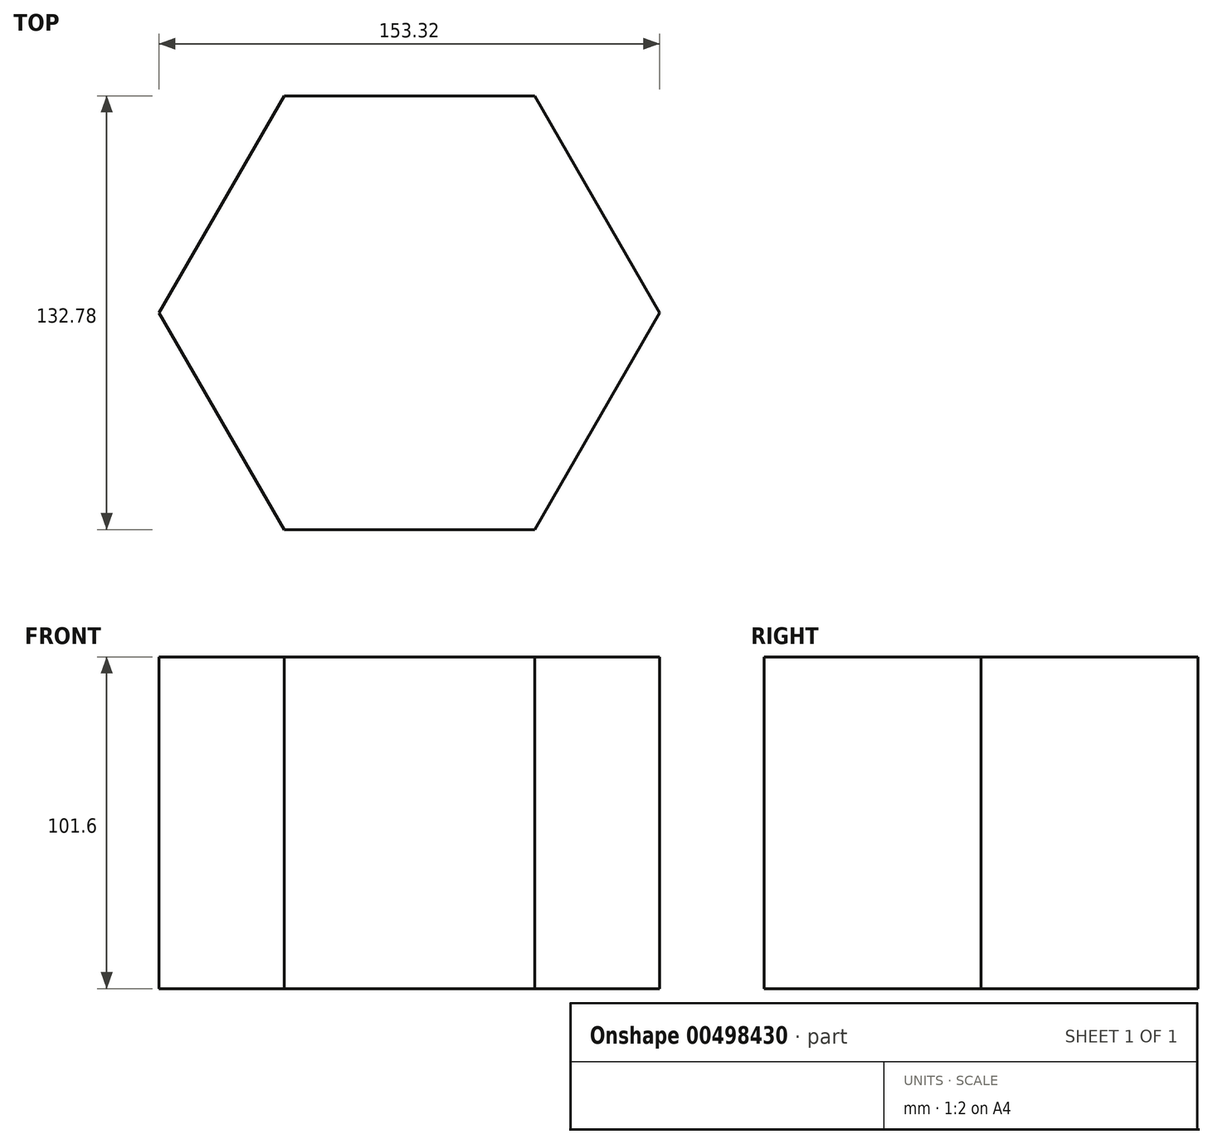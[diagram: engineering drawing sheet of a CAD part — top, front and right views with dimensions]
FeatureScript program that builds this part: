
annotation { "Feature Type Name" : "Feature", "Feature Type Description" : "" }
export const myFeature = defineFeature(function(context is Context, id is Id, definition is map)
    precondition{}
    {
        {
            var Q0;
            Q0=qCreatedBy(makeId("Top.planeOp"),FACE);
            var sketch = newSketch(context, id + "F0", { "sketchPlane" : qUnion([Q0])});
            skCircle(sketch, "E0.cCircle", {"center": v(0, 0) * mm, "radius": 76.66 * mm, "construction": true});
            skLineSegment(sketch, "E0.0", {"start": v(76.66, 0) * mm, "end": v(38.33, -66.39) * mm});
            skLineSegment(sketch, "E0.1", {"start": v(38.33, -66.39) * mm, "end": v(-38.33, -66.39) * mm});
            skLineSegment(sketch, "E0.2", {"start": v(-38.33, -66.39) * mm, "end": v(-76.66, 0) * mm});
            skLineSegment(sketch, "E0.3", {"start": v(-76.66, 0) * mm, "end": v(-38.33, 66.39) * mm});
            skLineSegment(sketch, "E0.4", {"start": v(-38.33, 66.39) * mm, "end": v(38.33, 66.39) * mm});
            skLineSegment(sketch, "E0.5", {"start": v(38.33, 66.39) * mm, "end": v(76.66, 0) * mm});
            skSolve(sketch);
        }
        {
            var Q0;
            Q0=makeQuery(id+"F0.imprint","IMPRINT",FACE,{"disambiguationData":[TD([[makeQuery(id+"F0.imprint","IMPRINT",EDGE,{"derivedFrom":sQuery(id+"F0.wireOp",EDGE,"E0.0")}),-1.0]])]});
            extrude(context, id + "F1", {"entities" : qUnion([Q0]), "depth" : 101.6 * mm, "offsetDistance" : 25.4 * mm});
        }
    });
